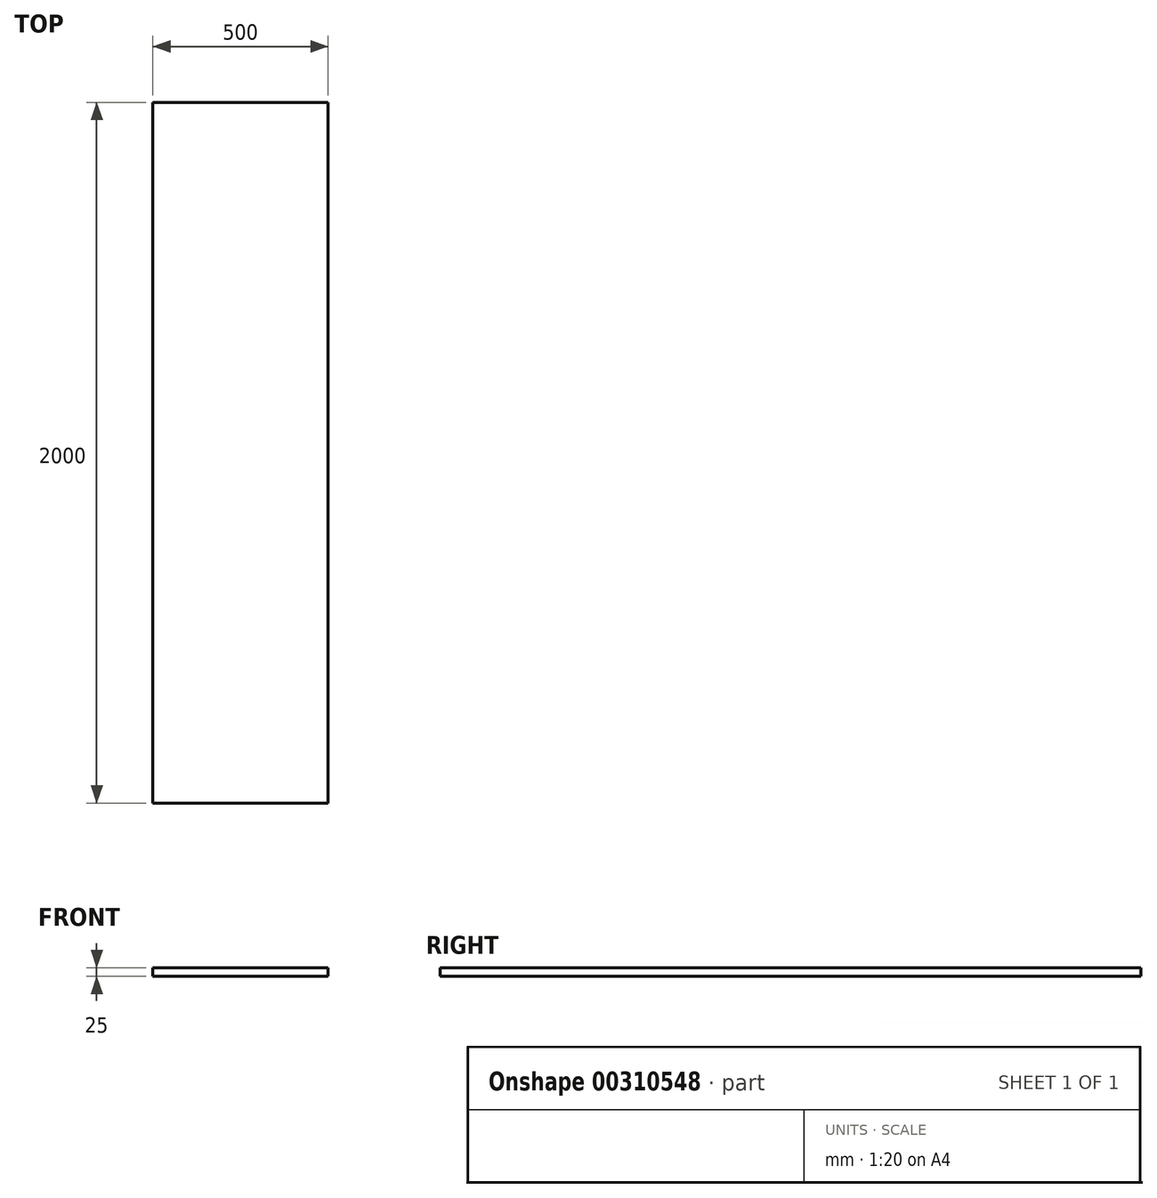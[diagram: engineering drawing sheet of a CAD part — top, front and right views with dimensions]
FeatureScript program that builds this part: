
annotation { "Feature Type Name" : "Feature", "Feature Type Description" : "" }
export const myFeature = defineFeature(function(context is Context, id is Id, definition is map)
    precondition{}
    {
        {
            var Q0;
            Q0=qCreatedBy(makeId("Top.planeOp"),FACE);
            var sketch = newSketch(context, id + "F0", { "sketchPlane" : qUnion([Q0])});
            skLineSegment(sketch, "E0.bottom", {"start": v(0, 0) * mm, "end": v(-500, 0) * mm});
            skLineSegment(sketch, "E0.top", {"start": v(0, -2000) * mm, "end": v(-500, -2000) * mm});
            skLineSegment(sketch, "E0.left", {"start": v(0, 0) * mm, "end": v(0, -2000) * mm});
            skLineSegment(sketch, "E0.right", {"start": v(-500, 0) * mm, "end": v(-500, -2000) * mm});
            skSolve(sketch);
        }
        {
            var Q0;
            Q0=makeQuery(id+"F0.imprint","IMPRINT",FACE,{"disambiguationData":[TD([[makeQuery(id+"F0.imprint","IMPRINT",EDGE,{"derivedFrom":sQuery(id+"F0.wireOp",EDGE,"E0.bottom")}),1.0]])]});
            extrude(context, id + "F1", {"entities" : qUnion([Q0]), "depth" : 25 * mm});
        }
    });
